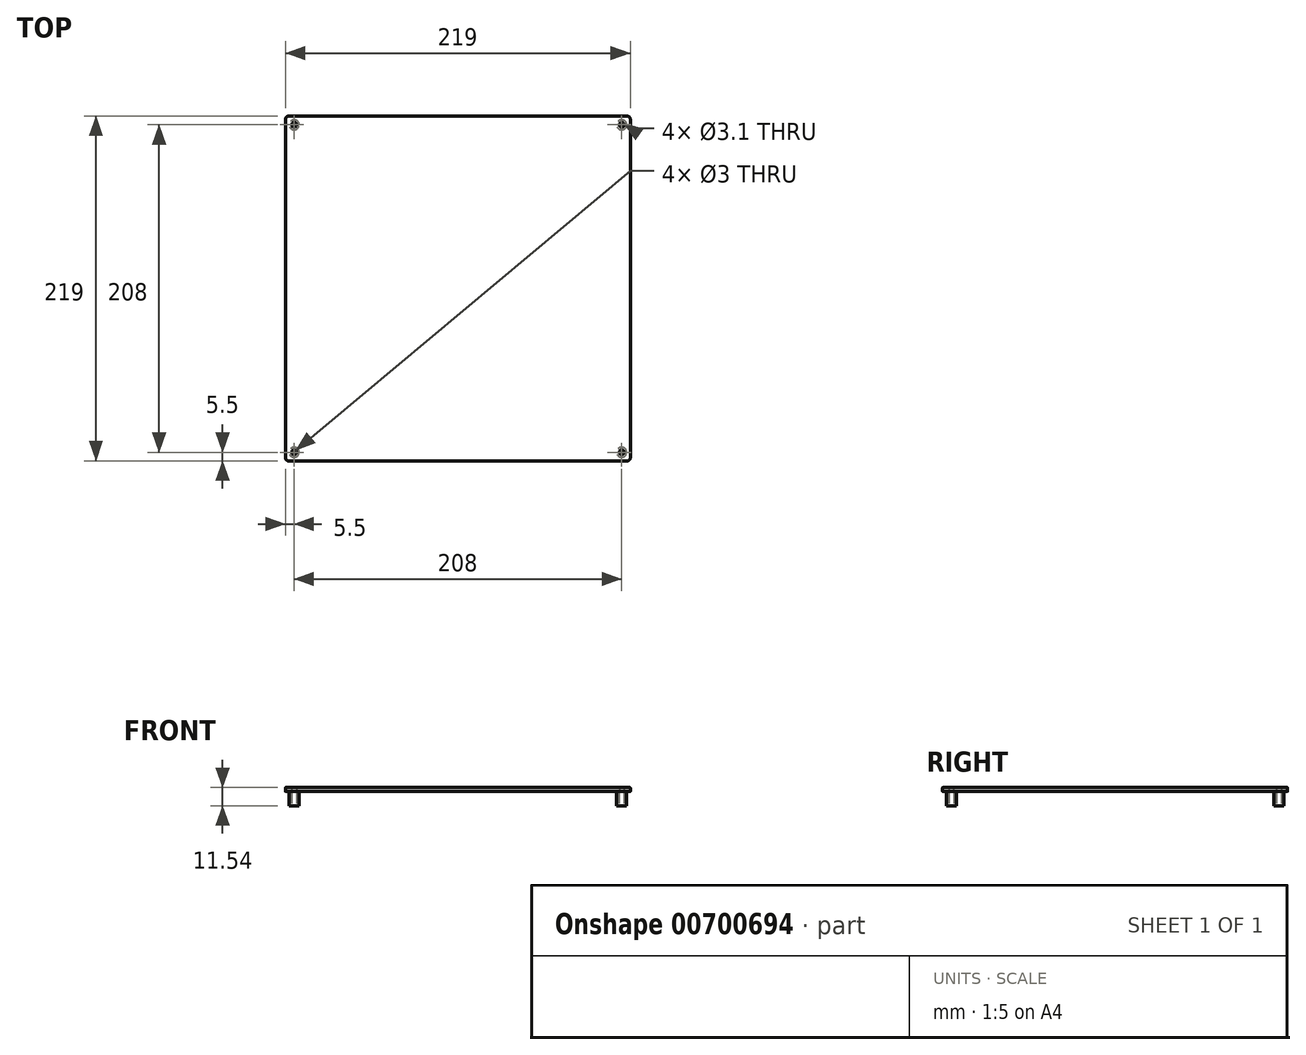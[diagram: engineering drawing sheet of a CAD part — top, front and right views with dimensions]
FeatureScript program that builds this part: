
annotation { "Feature Type Name" : "Feature", "Feature Type Description" : "" }
export const myFeature = defineFeature(function(context is Context, id is Id, definition is map)
    precondition{}
    {
        {
            var Q0;
            Q0=qCreatedBy(makeId("Top.planeOp"),FACE);
            var sketch = newSketch(context, id + "F0", { "sketchPlane" : qUnion([Q0])});
            skLineSegment(sketch, "E0.bottom", {"start": v(0, 0) * mm, "end": v(-219, 0) * mm});
            skLineSegment(sketch, "E0.top", {"start": v(0, -219) * mm, "end": v(-219, -219) * mm});
            skLineSegment(sketch, "E0.left", {"start": v(0, 0) * mm, "end": v(0, -219) * mm});
            skLineSegment(sketch, "E0.right", {"start": v(-219, 0) * mm, "end": v(-219, -219) * mm});
            skSolve(sketch);
        }
        {
            var Q0;
            Q0=makeQuery(id+"F0.imprint","IMPRINT",FACE,{"disambiguationData":[TD([[makeQuery(id+"F0.imprint","IMPRINT",EDGE,{"derivedFrom":sQuery(id+"F0.wireOp",EDGE,"E0.bottom")}),1.0]])]});
            var sketch = newSketch(context, id + "F1", { "sketchPlane" : qUnion([Q0])});
            skPoint(sketch, "E1", {"position": v(-5.5, -213.5) * mm});
            skPoint(sketch, "E2", {"position": v(-213.5, -213.5) * mm});
            skPoint(sketch, "E3", {"position": v(-213.5, -5.5) * mm});
            skPoint(sketch, "E4", {"position": v(-5.5, -5.5) * mm});
            skSolve(sketch);
        }
        {
            var Q0;
            Q0=makeQuery(id+"F0.imprint","IMPRINT",FACE,{"disambiguationData":[TD([[makeQuery(id+"F0.imprint","IMPRINT",EDGE,{"derivedFrom":sQuery(id+"F0.wireOp",EDGE,"E0.bottom")}),1.0]])]});
            extrude(context, id + "F2", {"entities" : qUnion([Q0]), "depth" : 2.54 * mm, "offsetDistance" : 25 * mm});
        }
        {
            var Q0;
            Q0=sQuery(id+"F1.wireOp",VERTEX,"E4");
            var Q1;
            Q1=sQuery(id+"F1.wireOp",VERTEX,"E1");
            var Q2;
            Q2=sQuery(id+"F1.wireOp",VERTEX,"E2");
            var Q3;
            Q3=sQuery(id+"F1.wireOp",VERTEX,"E3");
            var Q4;
            Q4=makeQuery(id+"F2.opExtrude","SWEPT_BODY",BODY,{"disambiguationData":[OSD([sQuery(id+"F0.wireOp",EDGE,"E0.bottom"),sQuery(id+"F0.wireOp",EDGE,"E0.top"),sQuery(id+"F0.wireOp",EDGE,"E0.left"),sQuery(id+"F0.wireOp",EDGE,"E0.right")])]});
            hole(context, id + "F3", {"style" : HoleStyle.SIMPLE, "endStyle" : HoleEndStyle.THROUGH, "oppositeDirection" : true, "holeDiameter" : 3 * mm, "isTappedThrough" : true, "tappedDepth" : 12 * mm, "tapClearance" : 3, "locations" : qUnion([Q0, Q1, Q2, Q3]), "scope" : qUnion([Q4])});
        }
        {
            var Q0;
            Q0=makeQuery(id+"F2.opExtrude","SWEPT_EDGE",EDGE,{"disambiguationData":[OSD([sQuery(id+"F0.wireOp",EDGE,"E0.top"),sQuery(id+"F0.wireOp",EDGE,"E0.right")])]});
            fillet(context, id + "F4", {"entities" : qUnion([Q0]), "radius" : 2 * mm, "tangentPropagation" : true, "allowEdgeOverflow" : false});
        }
        {
            var Q0;
            Q0=makeQuery(id+"F2.opExtrude","SWEPT_EDGE",EDGE,{"disambiguationData":[OSD([sQuery(id+"F0.wireOp",EDGE,"E0.bottom"),sQuery(id+"F0.wireOp",EDGE,"E0.right")])]});
            var Q1;
            Q1=makeQuery(id+"F2.opExtrude","SWEPT_EDGE",EDGE,{"disambiguationData":[OSD([sQuery(id+"F0.wireOp",EDGE,"E0.top"),sQuery(id+"F0.wireOp",EDGE,"E0.left")])]});
            fillet(context, id + "F5", {"entities" : qUnion([Q0, Q1]), "radius" : 2 * mm, "tangentPropagation" : true, "allowEdgeOverflow" : false});
        }
        {
            var Q0;
            Q0=makeQuery(id+"F2.opExtrude","SWEPT_EDGE",EDGE,{"disambiguationData":[OSD([sQuery(id+"F0.wireOp",EDGE,"E0.bottom"),sQuery(id+"F0.wireOp",EDGE,"E0.left")])]});
            fillet(context, id + "F6", {"entities" : qUnion([Q0]), "radius" : 2 * mm, "tangentPropagation" : true, "allowEdgeOverflow" : false});
        }
        {
            var Q0;
            Q0=makeQuery(id+"F2.opExtrude","CAP_EDGE",EDGE,{"disambiguationData":[OSD([sQuery(id+"F0.wireOp",EDGE,"E0.top")])],"isStart":false});
            fillet(context, id + "F7", {"entities" : qUnion([Q0]), "radius" : .1 * mm, "tangentPropagation" : true, "allowEdgeOverflow" : false});
        }
        {
            var Q0;
            Q0=makeQuery(id+"F2.opExtrude","CAP_EDGE",EDGE,{"disambiguationData":[OSD([sQuery(id+"F0.wireOp",EDGE,"E0.right")])],"isStart":true});
            fillet(context, id + "F8", {"entities" : qUnion([Q0]), "radius" : .1 * mm, "tangentPropagation" : true, "allowEdgeOverflow" : false});
        }
        {
            var Q0;
            Q0=makeQuery(id+"F2.opExtrude","SWEPT_BODY",BODY,{"disambiguationData":[OSD([sQuery(id+"F0.wireOp",EDGE,"E0.bottom"),sQuery(id+"F0.wireOp",EDGE,"E0.top"),sQuery(id+"F0.wireOp",EDGE,"E0.left"),sQuery(id+"F0.wireOp",EDGE,"E0.right")])]});
            transform(context, id + "F9", {"entities" : qUnion([Q0]), "transformType" : TransformType.TRANSLATION_3D, "dx" : 0 * mm, "dy" : 0 * mm, "dz" : 9 * mm, "makeCopy" : true});
        }
        {
            var Q0;
            Q0=qCreatedBy(makeId("Top.planeOp"),FACE);
            var sketch = newSketch(context, id + "F10", { "sketchPlane" : qUnion([Q0])});
            skCircle(sketch, "E5", {"center": v(0, 0) * mm, "radius": 3.17 * mm});
            skCircle(sketch, "E6", {"center": v(0, 0) * mm, "radius": 1.55 * mm});
            skSolve(sketch);
        }
        {
            var Q0;
            Q0=makeQuery(id+"F10.imprint","IMPRINT",FACE,{"disambiguationData":[TD([[makeQuery(id+"F10.imprint","IMPRINT",EDGE,{"derivedFrom":sQuery(id+"F10.wireOp",EDGE,"E5")}),1.0]])]});
            extrude(context, id + "F11", {"entities" : qUnion([Q0]), "depth" : 9 * mm, "offsetDistance" : 25 * mm});
        }
        {
            var Q0;
            Q0=makeQuery(id+"F2.opExtrude","SWEPT_BODY",BODY,{"disambiguationData":[OSD([sQuery(id+"F0.wireOp",EDGE,"E0.bottom"),sQuery(id+"F0.wireOp",EDGE,"E0.top"),sQuery(id+"F0.wireOp",EDGE,"E0.left"),sQuery(id+"F0.wireOp",EDGE,"E0.right")])]});
            transform(context, id + "F12", {"entities" : qUnion([Q0]), "transformType" : TransformType.TRANSLATION_3D, "dx" : 0 * mm, "dy" : 0 * mm, "dz" : -2.54 * mm, "makeCopy" : false});
        }
        {
            var Q0;
            Q0=makeQuery(id+"F11.opExtrude","SWEPT_BODY",BODY,{"disambiguationData":[OSD([sQuery(id+"F10.wireOp",EDGE,"E5"),sQuery(id+"F10.wireOp",EDGE,"E6")])]});
            transform(context, id + "F13", {"entities" : qUnion([Q0]), "transformType" : TransformType.TRANSLATION_3D, "dx" : -5.5 * mm, "dy" : -5.5 * mm, "dz" : 0 * mm, "makeCopy" : false});
        }
        {
            var Q0;
            Q0=makeQuery(id+"F11.opExtrude","SWEPT_BODY",BODY,{"disambiguationData":[OSD([sQuery(id+"F10.wireOp",EDGE,"E5"),sQuery(id+"F10.wireOp",EDGE,"E6")])]});
            transform(context, id + "F14", {"entities" : qUnion([Q0]), "transformType" : TransformType.TRANSLATION_3D, "dx" : 0 * mm, "dy" : -208 * mm, "dz" : 0 * mm, "makeCopy" : true});
        }
        {
            var Q0;
            Q0=makeQuery(id+"F14.opPattern","COPY",BODY,{"derivedFrom":makeQuery(id+"F11.opExtrude","SWEPT_BODY",BODY,{"disambiguationData":[OSD([sQuery(id+"F10.wireOp",EDGE,"E5"),sQuery(id+"F10.wireOp",EDGE,"E6")])]}),"instanceName":"1"});
            transform(context, id + "F15", {"entities" : qUnion([Q0]), "transformType" : TransformType.TRANSLATION_3D, "dx" : -208 * mm, "dy" : 0 * mm, "dz" : 0 * mm, "makeCopy" : true});
        }
        {
            var Q0;
            Q0=makeQuery(id+"F15.opPattern","COPY",BODY,{"derivedFrom":makeQuery(id+"F14.opPattern","COPY",BODY,{"derivedFrom":makeQuery(id+"F11.opExtrude","SWEPT_BODY",BODY,{"disambiguationData":[OSD([sQuery(id+"F10.wireOp",EDGE,"E5"),sQuery(id+"F10.wireOp",EDGE,"E6")])]}),"instanceName":"1"}),"instanceName":"1"});
            transform(context, id + "F16", {"entities" : qUnion([Q0]), "transformType" : TransformType.TRANSLATION_3D, "dx" : 0 * mm, "dy" : 208 * mm, "dz" : 0 * mm, "makeCopy" : true});
        }
        {
            var Q0;
            Q0=makeQuery(id+"F2.opExtrude","CAP_FACE",FACE,{"disambiguationData":[OSD([sQuery(id+"F0.wireOp",EDGE,"E0.bottom"),sQuery(id+"F0.wireOp",EDGE,"E0.top"),sQuery(id+"F0.wireOp",EDGE,"E0.left"),sQuery(id+"F0.wireOp",EDGE,"E0.right")])],"isStart":true});
            var sketch = newSketch(context, id + "F17", { "sketchPlane" : qUnion([Q0])});
            skLineSegment(sketch, "E7.bottom", {"start": v(-199.4, 199.4) * mm, "end": v(-19.6, 199.4) * mm, "construction": true});
            skLineSegment(sketch, "E7.top", {"start": v(-199.4, 19.6) * mm, "end": v(-19.6, 19.6) * mm, "construction": true});
            skLineSegment(sketch, "E7.left", {"start": v(-199.4, 199.4) * mm, "end": v(-199.4, 19.6) * mm, "construction": true});
            skLineSegment(sketch, "E7.right", {"start": v(-19.6, 199.4) * mm, "end": v(-19.6, 19.6) * mm, "construction": true});
            skLineSegment(sketch, "E8.bottom", {"start": v(-199.4, 199.4) * mm, "end": v(-19.6, 199.4) * mm});
            skLineSegment(sketch, "E8.top", {"start": v(-199.4, 19.6) * mm, "end": v(-19.6, 19.6) * mm});
            skLineSegment(sketch, "E8.left", {"start": v(-199.4, 199.4) * mm, "end": v(-199.4, 19.6) * mm});
            skLineSegment(sketch, "E8.right", {"start": v(-19.6, 199.4) * mm, "end": v(-19.6, 19.6) * mm});
            skSolve(sketch);
        }
        {
            var Q0;
            Q0=makeQuery(id+"F17.imprint","IMPRINT",FACE,{"disambiguationData":[TD([[makeQuery(id+"F17.imprint","IMPRINT",EDGE,{"derivedFrom":sQuery(id+"F17.wireOp",EDGE,"E8.bottom")}),-1.0]])]});
            extrude(context, id + "F18", {"entities" : qUnion([Q0]), "operationType" : NewBodyOperationType.REMOVE, "oppositeDirection" : true, "depth" : .5 * mm, "offsetDistance" : 25 * mm});
        }
        {
            var Q0;
            Q0=makeQuery(id+"F2.opExtrude","SWEPT_BODY",BODY,{"disambiguationData":[OSD([sQuery(id+"F0.wireOp",EDGE,"E0.bottom"),sQuery(id+"F0.wireOp",EDGE,"E0.top"),sQuery(id+"F0.wireOp",EDGE,"E0.left"),sQuery(id+"F0.wireOp",EDGE,"E0.right")])]});
            deleteBodies(context, id + "F19", {"entities" : qUnion([Q0])});
        }
    });
